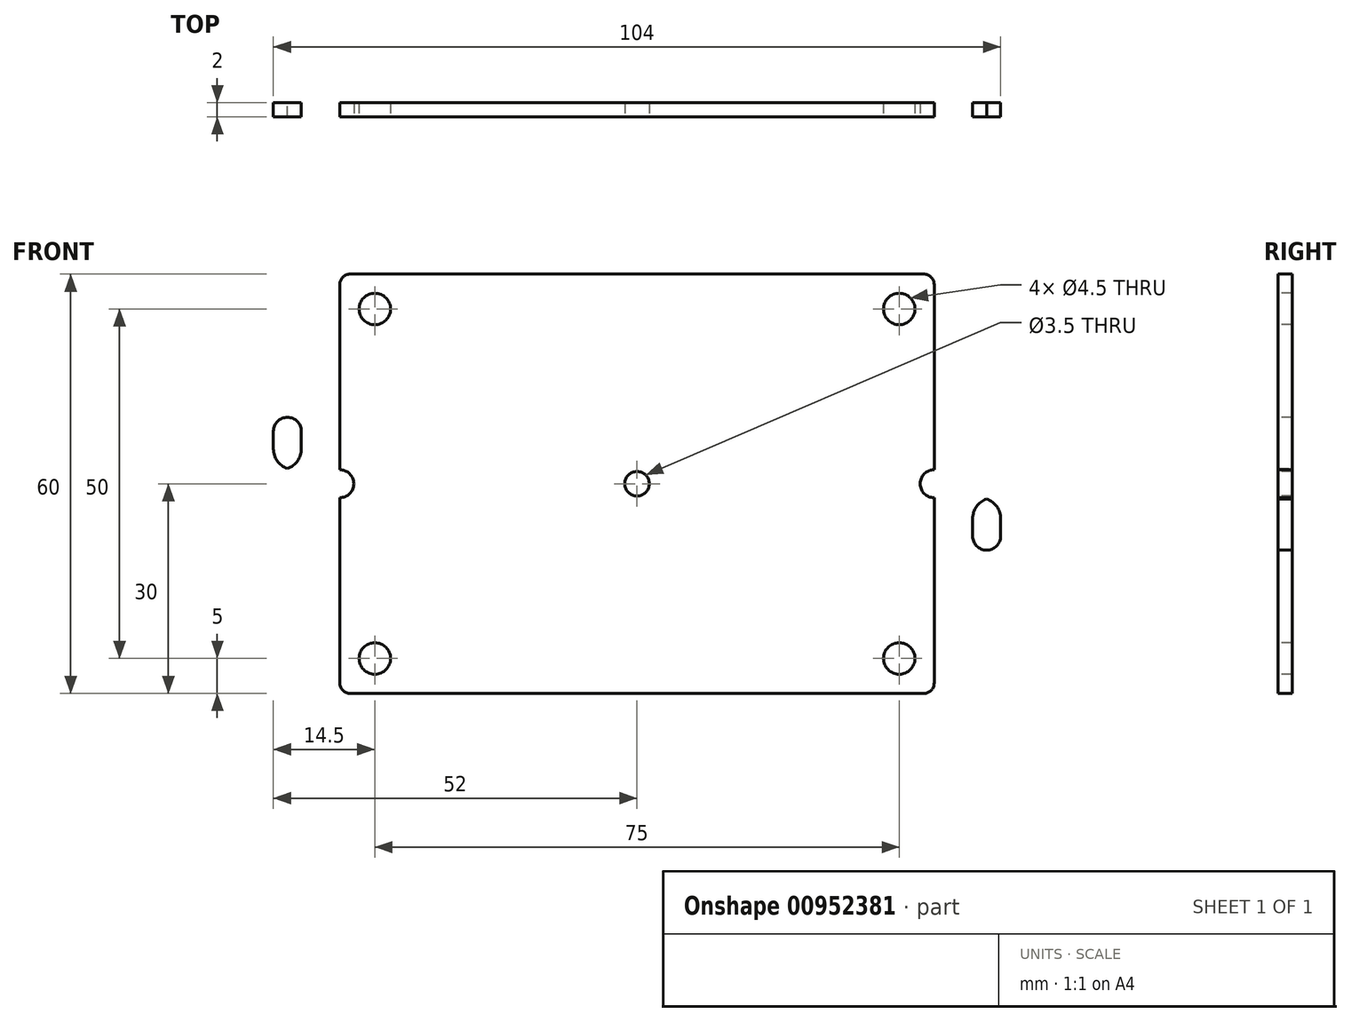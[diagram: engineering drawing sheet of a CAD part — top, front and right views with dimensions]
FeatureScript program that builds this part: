
annotation { "Feature Type Name" : "Feature", "Feature Type Description" : "" }
export const myFeature = defineFeature(function(context is Context, id is Id, definition is map)
    precondition{}
    {
        {
            var Q0;
            Q0=qCreatedBy(makeId("Front.planeOp"),FACE);
            var sketch = newSketch(context, id + "F0", { "sketchPlane" : qUnion([Q0])});
            skLineSegment(sketch, "E0.bottom", {"start": v(-42.5, -30) * mm, "end": v(42.5, -30) * mm});
            skLineSegment(sketch, "E0.top", {"start": v(-42.5, 30) * mm, "end": v(42.5, 30) * mm});
            skLineSegment(sketch, "E0.left", {"start": v(-42.5, -30) * mm, "end": v(-42.5, 30) * mm});
            skLineSegment(sketch, "E0.right", {"start": v(42.5, -30) * mm, "end": v(42.5, 30) * mm});
            skCircle(sketch, "E1", {"center": v(-37.5, 25) * mm, "radius": 2.25 * mm});
            skCircle(sketch, "E2", {"center": v(37.5, 25) * mm, "radius": 2.25 * mm});
            skCircle(sketch, "E3", {"center": v(-37.5, -25) * mm, "radius": 2.25 * mm});
            skCircle(sketch, "E4", {"center": v(37.5, -25) * mm, "radius": 2.25 * mm});
            skCircle(sketch, "E5", {"center": v(0, 0) * mm, "radius": 1.75 * mm});
            skLineSegment(sketch, "E6", {"start": v(-50, 7.5) * mm, "end": v(-50, -7.5) * mm});
            skLineSegment(sketch, "E7", {"start": v(-57.5, 0) * mm, "end": v(-42.5, 0) * mm});
            skArc(sketch, "E8.0.startCap", {"start": v(-52, 7.5) * mm, "mid": v(-50, 9.5) * mm, "end": v(-48, 7.5) * mm});
            skArc(sketch, "E8.0.endCap", {"start": v(-48, -7.5) * mm, "mid": v(-50, -9.5) * mm, "end": v(-52, -7.5) * mm});
            skLineSegment(sketch, "E8.0.left", {"start": v(-48, 7.5) * mm, "end": v(-48, -7.5) * mm});
            skLineSegment(sketch, "E8.0.right", {"start": v(-52, 7.5) * mm, "end": v(-52, -7.5) * mm});
            skArc(sketch, "E8.1.startCap", {"start": v(-57.5, -2) * mm, "mid": v(-59.5, 0) * mm, "end": v(-57.5, 2) * mm});
            skArc(sketch, "E8.1.endCap", {"start": v(-42.5, 2) * mm, "mid": v(-40.5, 0) * mm, "end": v(-42.5, -2) * mm});
            skLineSegment(sketch, "E8.1.left", {"start": v(-57.5, 2) * mm, "end": v(-42.5, 2) * mm});
            skLineSegment(sketch, "E8.1.right", {"start": v(-57.5, -2) * mm, "end": v(-42.5, -2) * mm});
            skArc(sketch, "E9.1.0.0", {"start": v(52, -7.5) * mm, "mid": v(50, -9.5) * mm, "end": v(48, -7.5) * mm});
            skArc(sketch, "E9.1.0.1", {"start": v(48, 7.5) * mm, "mid": v(50, 9.5) * mm, "end": v(52, 7.5) * mm});
            skLineSegment(sketch, "E9.1.0.2", {"start": v(52, 7.5) * mm, "end": v(52, -7.5) * mm});
            skLineSegment(sketch, "E9.1.0.3", {"start": v(42.5, 2) * mm, "end": v(57.5, 2) * mm});
            skLineSegment(sketch, "E9.1.0.4", {"start": v(42.5, -2) * mm, "end": v(57.5, -2) * mm});
            skLineSegment(sketch, "E9.1.0.5", {"start": v(42.5, 0) * mm, "end": v(57.5, 0) * mm});
            skLineSegment(sketch, "E9.1.0.6", {"start": v(48, 7.5) * mm, "end": v(48, -7.5) * mm});
            skArc(sketch, "E9.1.0.7", {"start": v(57.5, 2) * mm, "mid": v(59.5, 0) * mm, "end": v(57.5, -2) * mm});
            skLineSegment(sketch, "E9.1.0.8", {"start": v(50, 7.5) * mm, "end": v(50, -7.5) * mm});
            skArc(sketch, "E9.1.0.9", {"start": v(42.5, -2) * mm, "mid": v(40.5, 0) * mm, "end": v(42.5, 2) * mm});
            skLineSegment(sketch, "E9.direction1", {"start": v(-52, -7.5) * mm, "end": v(48, -7.5) * mm, "construction": true});
            skLineSegment(sketch, "E10.bottom", {"start": v(-65, 15) * mm, "end": v(65, 15) * mm});
            skLineSegment(sketch, "E10.top", {"start": v(-65, -15) * mm, "end": v(65, -15) * mm});
            skLineSegment(sketch, "E10.left", {"start": v(-65, 15) * mm, "end": v(-65, -15) * mm});
            skLineSegment(sketch, "E10.right", {"start": v(65, 15) * mm, "end": v(65, -15) * mm});
            skSolve(sketch);
        }
        {
            var Q0;
            Q0=makeQuery(id+"F0.imprint","IMPRINT",FACE,{"disambiguationData":[TD([[makeQuery(id+"F0.imprint","IMPRINT",EDGE,{"derivedFrom":sQuery(id+"F0.wireOp",EDGE,"E2")}),-1.0]])]});
            var Q1;
            Q1=makeQuery(id+"F0.imprint","IMPRINT",FACE,{"disambiguationData":[TD([[makeQuery(id+"F0.imprint","IMPRINT",EDGE,{"derivedFrom":sQuery(id+"F0.wireOp",EDGE,"E4")}),-1.0]])]});
            var Q2;
            {var subQ0=sQuery(id+"F0.wireOp",EDGE,"rjaW78t7-ypJx-lVJN-FZRe-d6buYRmC77cn");Q2=makeQuery(id+"F0.imprint","IMPRINT",FACE,{"disambiguationData":[TD([[makeQuery(id+"F0.imprint","IMPRINT",EDGE,{"derivedFrom":subQ0}),-1.0]])]});}
            var Q3;
            {var subQ0=sQuery(id+"F0.wireOp",EDGE,"1NJd6Qoc-oje8-l9O0-L9cF-t73cIRtufikx");Q3=makeQuery(id+"F0.imprint","IMPRINT",FACE,{"disambiguationData":[TD([[makeQuery(id+"F0.imprint","IMPRINT",EDGE,{"derivedFrom":subQ0}),1.0]])]});}
            var Q4;
            Q4=makeQuery(id+"F0.imprint","IMPRINT",FACE,{"disambiguationData":[TD([[makeQuery(id+"F0.imprint","IMPRINT",EDGE,{"derivedFrom":sQuery(id+"F0.wireOp",EDGE,"E3OZl69u-UJ4j-6qNk-wf2I-6YzBL0ODdr67")}),-1.0]])]});
            var Q5;
            {var subQ0=sQuery(id+"F0.wireOp",EDGE,"PN9uGExE-e6ce-JM7U-WgBa-r8B8Oa9EvhlK");var subQ1=sQuery(id+"F0.wireOp",EDGE,"r9N8xMkt-jfr5-NPvg-kqhV-x66qSIRX31zV");var subQ2=makeQuery(id+"F0.imprint","INTERSECT",VERTEX,{"disambiguationData":[OD(0.0)],"derivedFrom":[subQ1,subQ0]});Q5=makeQuery(id+"F0.imprint","IMPRINT",FACE,{"disambiguationData":[TD([[makeQuery(id+"F0.imprint","IMPRINT",EDGE,{"disambiguationData":[TD([[subQ2,-1.0]])],"derivedFrom":subQ0}),1.0]])]});}
            var Q6;
            {var subQ0=sQuery(id+"F0.wireOp",EDGE,"PN9uGExE-e6ce-JM7U-WgBa-r8B8Oa9EvhlK");var subQ1=sQuery(id+"F0.wireOp",EDGE,"r9N8xMkt-jfr5-NPvg-kqhV-x66qSIRX31zV");var subQ2=makeQuery(id+"F0.imprint","INTERSECT",VERTEX,{"disambiguationData":[OD(1.0)],"derivedFrom":[subQ1,subQ0]});Q6=makeQuery(id+"F0.imprint","IMPRINT",FACE,{"disambiguationData":[TD([[makeQuery(id+"F0.imprint","IMPRINT",EDGE,{"disambiguationData":[TD([[subQ2,1.0]])],"derivedFrom":subQ0}),1.0]])]});}
            var Q7;
            {var subQ0=sQuery(id+"F0.wireOp",EDGE,"9v4P5pMU-RGOu-vqJf-tuKl-UVKpjkJdRUzS");var subQ1=sQuery(id+"F0.wireOp",EDGE,"65dx6mvX-bEGy-U7NT-FcBn-9mAAU7fRP4gA");var subQ2=makeQuery(id+"F0.imprint","INTERSECT",VERTEX,{"disambiguationData":[OD(1.0)],"derivedFrom":[subQ1,subQ0]});Q7=makeQuery(id+"F0.imprint","IMPRINT",FACE,{"disambiguationData":[TD([[makeQuery(id+"F0.imprint","IMPRINT",EDGE,{"disambiguationData":[TD([[subQ2,-1.0]])],"derivedFrom":subQ1}),-1.0]])]});}
            var Q8;
            {var subQ0=sQuery(id+"F0.wireOp",EDGE,"9v4P5pMU-RGOu-vqJf-tuKl-UVKpjkJdRUzS");var subQ1=sQuery(id+"F0.wireOp",EDGE,"65dx6mvX-bEGy-U7NT-FcBn-9mAAU7fRP4gA");var subQ2=makeQuery(id+"F0.imprint","INTERSECT",VERTEX,{"disambiguationData":[OD(1.0)],"derivedFrom":[subQ1,subQ0]});Q8=makeQuery(id+"F0.imprint","IMPRINT",FACE,{"disambiguationData":[TD([[makeQuery(id+"F0.imprint","IMPRINT",EDGE,{"disambiguationData":[TD([[subQ2,-1.0]])],"derivedFrom":subQ1}),1.0]])]});}
            var Q9;
            {var subQ0=sQuery(id+"F0.wireOp",EDGE,"hM2ZLU3s-uU6V-4ag1-q0J9-zNWtTk9yT7fe");var subQ1=sQuery(id+"F0.wireOp",EDGE,"r9N8xMkt-jfr5-NPvg-kqhV-x66qSIRX31zV");var subQ2=makeQuery(id+"F0.imprint","INTERSECT",VERTEX,{"disambiguationData":[OD(1.0)],"derivedFrom":[subQ1,subQ0]});Q9=makeQuery(id+"F0.imprint","IMPRINT",FACE,{"disambiguationData":[TD([[makeQuery(id+"F0.imprint","IMPRINT",EDGE,{"disambiguationData":[TD([[subQ2,-1.0]])],"derivedFrom":subQ1}),-1.0]])]});}
            var Q10;
            {var subQ0=sQuery(id+"F0.wireOp",EDGE,"wBLZlDLe-3T5N-0JWb-rmkb-ln4iytn4BMBR");var subQ1=sQuery(id+"F0.wireOp",EDGE,"r9N8xMkt-jfr5-NPvg-kqhV-x66qSIRX31zV");var subQ2=makeQuery(id+"F0.imprint","INTERSECT",VERTEX,{"disambiguationData":[OD(1.0)],"derivedFrom":[subQ1,subQ0]});Q10=makeQuery(id+"F0.imprint","IMPRINT",FACE,{"disambiguationData":[TD([[makeQuery(id+"F0.imprint","IMPRINT",EDGE,{"disambiguationData":[TD([[subQ2,-1.0]])],"derivedFrom":subQ1}),-1.0]])]});}
            var Q11;
            {var subQ0=sQuery(id+"F0.wireOp",EDGE,"hM2ZLU3s-uU6V-4ag1-q0J9-zNWtTk9yT7fe");var subQ1=sQuery(id+"F0.wireOp",EDGE,"r9N8xMkt-jfr5-NPvg-kqhV-x66qSIRX31zV");var subQ2=makeQuery(id+"F0.imprint","INTERSECT",VERTEX,{"disambiguationData":[OD(0.0)],"derivedFrom":[subQ1,subQ0]});Q11=makeQuery(id+"F0.imprint","IMPRINT",FACE,{"disambiguationData":[TD([[makeQuery(id+"F0.imprint","IMPRINT",EDGE,{"disambiguationData":[TD([[subQ2,-1.0]])],"derivedFrom":subQ1}),-1.0]])]});}
            var Q12;
            {var subQ0=sQuery(id+"F0.wireOp",EDGE,"hM2ZLU3s-uU6V-4ag1-q0J9-zNWtTk9yT7fe");var subQ1=sQuery(id+"F0.wireOp",EDGE,"r9N8xMkt-jfr5-NPvg-kqhV-x66qSIRX31zV");var subQ2=makeQuery(id+"F0.imprint","INTERSECT",VERTEX,{"disambiguationData":[OD(0.0)],"derivedFrom":[subQ1,subQ0]});Q12=makeQuery(id+"F0.imprint","IMPRINT",FACE,{"disambiguationData":[TD([[makeQuery(id+"F0.imprint","IMPRINT",EDGE,{"disambiguationData":[TD([[subQ2,-1.0]])],"derivedFrom":subQ1}),1.0]])]});}
            var Q13;
            {var subQ0=sQuery(id+"F0.wireOp",EDGE,"wBLZlDLe-3T5N-0JWb-rmkb-ln4iytn4BMBR");var subQ1=sQuery(id+"F0.wireOp",EDGE,"r9N8xMkt-jfr5-NPvg-kqhV-x66qSIRX31zV");var subQ2=makeQuery(id+"F0.imprint","INTERSECT",VERTEX,{"disambiguationData":[OD(1.0)],"derivedFrom":[subQ1,subQ0]});Q13=makeQuery(id+"F0.imprint","IMPRINT",FACE,{"disambiguationData":[TD([[makeQuery(id+"F0.imprint","IMPRINT",EDGE,{"disambiguationData":[TD([[subQ2,-1.0]])],"derivedFrom":subQ1}),1.0]])]});}
            var Q14;
            {var subQ0=sQuery(id+"F0.wireOp",EDGE,"hM2ZLU3s-uU6V-4ag1-q0J9-zNWtTk9yT7fe");var subQ1=sQuery(id+"F0.wireOp",EDGE,"r9N8xMkt-jfr5-NPvg-kqhV-x66qSIRX31zV");var subQ2=makeQuery(id+"F0.imprint","INTERSECT",VERTEX,{"disambiguationData":[OD(0.0)],"derivedFrom":[subQ1,subQ0]});Q14=makeQuery(id+"F0.imprint","IMPRINT",FACE,{"disambiguationData":[TD([[makeQuery(id+"F0.imprint","IMPRINT",EDGE,{"disambiguationData":[TD([[subQ2,1.0]])],"derivedFrom":subQ1}),-1.0]])]});}
            var Q15;
            {var subQ0=sQuery(id+"F0.wireOp",EDGE,"hM2ZLU3s-uU6V-4ag1-q0J9-zNWtTk9yT7fe");var subQ1=sQuery(id+"F0.wireOp",EDGE,"r9N8xMkt-jfr5-NPvg-kqhV-x66qSIRX31zV");var subQ2=makeQuery(id+"F0.imprint","INTERSECT",VERTEX,{"disambiguationData":[OD(0.0)],"derivedFrom":[subQ1,subQ0]});Q15=makeQuery(id+"F0.imprint","IMPRINT",FACE,{"disambiguationData":[TD([[makeQuery(id+"F0.imprint","IMPRINT",EDGE,{"disambiguationData":[TD([[subQ2,1.0]])],"derivedFrom":subQ1}),1.0]])]});}
            var Q16;
            {var subQ0=sQuery(id+"F0.wireOp",EDGE,"tNTzekTW-7BOb-6XFC-JdlP-r3fOIQGOdmsq");var subQ1=sQuery(id+"F0.wireOp",EDGE,"65dx6mvX-bEGy-U7NT-FcBn-9mAAU7fRP4gA");var subQ2=makeQuery(id+"F0.imprint","INTERSECT",VERTEX,{"disambiguationData":[OD(0.0)],"derivedFrom":[subQ1,subQ0]});Q16=makeQuery(id+"F0.imprint","IMPRINT",FACE,{"disambiguationData":[TD([[makeQuery(id+"F0.imprint","IMPRINT",EDGE,{"disambiguationData":[TD([[subQ2,-1.0]])],"derivedFrom":subQ1}),1.0]])]});}
            var Q17;
            {var subQ0=sQuery(id+"F0.wireOp",EDGE,"tNTzekTW-7BOb-6XFC-JdlP-r3fOIQGOdmsq");var subQ1=sQuery(id+"F0.wireOp",EDGE,"65dx6mvX-bEGy-U7NT-FcBn-9mAAU7fRP4gA");var subQ2=makeQuery(id+"F0.imprint","INTERSECT",VERTEX,{"disambiguationData":[OD(0.0)],"derivedFrom":[subQ1,subQ0]});Q17=makeQuery(id+"F0.imprint","IMPRINT",FACE,{"disambiguationData":[TD([[makeQuery(id+"F0.imprint","IMPRINT",EDGE,{"disambiguationData":[TD([[subQ2,-1.0]])],"derivedFrom":subQ1}),-1.0]])]});}
            var Q18;
            {var subQ0=sQuery(id+"F0.wireOp",EDGE,"PN9uGExE-e6ce-JM7U-WgBa-r8B8Oa9EvhlK");var subQ1=sQuery(id+"F0.wireOp",EDGE,"r9N8xMkt-jfr5-NPvg-kqhV-x66qSIRX31zV");var subQ2=makeQuery(id+"F0.imprint","INTERSECT",VERTEX,{"disambiguationData":[OD(0.0)],"derivedFrom":[subQ1,subQ0]});Q18=makeQuery(id+"F0.imprint","IMPRINT",FACE,{"disambiguationData":[TD([[makeQuery(id+"F0.imprint","IMPRINT",EDGE,{"disambiguationData":[TD([[subQ2,-1.0]])],"derivedFrom":subQ1}),1.0]])]});}
            var Q19;
            {var subQ0=sQuery(id+"F0.wireOp",EDGE,"PN9uGExE-e6ce-JM7U-WgBa-r8B8Oa9EvhlK");var subQ1=sQuery(id+"F0.wireOp",EDGE,"r9N8xMkt-jfr5-NPvg-kqhV-x66qSIRX31zV");var subQ2=makeQuery(id+"F0.imprint","INTERSECT",VERTEX,{"disambiguationData":[OD(1.0)],"derivedFrom":[subQ1,subQ0]});Q19=makeQuery(id+"F0.imprint","IMPRINT",FACE,{"disambiguationData":[TD([[makeQuery(id+"F0.imprint","IMPRINT",EDGE,{"disambiguationData":[TD([[subQ2,1.0]])],"derivedFrom":subQ1}),1.0]])]});}
            var Q20;
            {var subQ0=sQuery(id+"F0.wireOp",EDGE,"hM2ZLU3s-uU6V-4ag1-q0J9-zNWtTk9yT7fe");var subQ1=sQuery(id+"F0.wireOp",EDGE,"r9N8xMkt-jfr5-NPvg-kqhV-x66qSIRX31zV");var subQ2=makeQuery(id+"F0.imprint","INTERSECT",VERTEX,{"disambiguationData":[OD(1.0)],"derivedFrom":[subQ1,subQ0]});Q20=makeQuery(id+"F0.imprint","IMPRINT",FACE,{"disambiguationData":[TD([[makeQuery(id+"F0.imprint","IMPRINT",EDGE,{"disambiguationData":[TD([[subQ2,-1.0]])],"derivedFrom":subQ1}),1.0]])]});}
            var Q21;
            Q21=makeQuery(id+"F0.imprint","IMPRINT",FACE,{"disambiguationData":[TD([[makeQuery(id+"F0.imprint","IMPRINT",EDGE,{"derivedFrom":sQuery(id+"F0.wireOp",EDGE,"E5")}),-1.0]])]});
            var Q22;
            {var subQ2=sQuery(id+"F0.wireOp",EDGE,"E8.0.startCap");Q22=makeQuery(id+"F0.imprint","IMPRINT",FACE,{"disambiguationData":[TD([[makeQuery(id+"F0.imprint","IMPRINT",EDGE,{"derivedFrom":subQ2}),1.0]])]});}
            var Q23;
            {var subQ7=sQuery(id+"F0.wireOp",EDGE,"E9.1.0.0");Q23=makeQuery(id+"F0.imprint","IMPRINT",FACE,{"disambiguationData":[TD([[makeQuery(id+"F0.imprint","IMPRINT",EDGE,{"derivedFrom":subQ7}),1.0]])]});}
            extrude(context, id + "F1", {"entities" : qUnion([Q0, Q1, Q2, Q3, Q4, Q5, Q6, Q7, Q8, Q9, Q10, Q11, Q12, Q13, Q14, Q15, Q16, Q17, Q18, Q19, Q20, Q21, Q22, Q23]), "oppositeDirection" : true, "depth" : 2 * mm, "offsetDistance" : 25 * mm});
        }
        {
            var Q0;
            Q0=makeQuery(id+"F1.opExtrude","SWEPT_EDGE",EDGE,{"disambiguationData":[OSD([sQuery(id+"F0.wireOp",EDGE,"E0.top"),sQuery(id+"F0.wireOp",EDGE,"E0.left")])]});
            var Q1;
            Q1=makeQuery(id+"F1.opExtrude","SWEPT_EDGE",EDGE,{"disambiguationData":[OSD([sQuery(id+"F0.wireOp",EDGE,"E0.top"),sQuery(id+"F0.wireOp",EDGE,"E0.right")])]});
            var Q2;
            Q2=makeQuery(id+"F1.opExtrude","SWEPT_EDGE",EDGE,{"disambiguationData":[OSD([sQuery(id+"F0.wireOp",EDGE,"E0.bottom"),sQuery(id+"F0.wireOp",EDGE,"E0.right")])]});
            var Q3;
            Q3=makeQuery(id+"F1.opExtrude","SWEPT_EDGE",EDGE,{"disambiguationData":[OSD([sQuery(id+"F0.wireOp",EDGE,"E0.bottom"),sQuery(id+"F0.wireOp",EDGE,"E0.left")])]});
            var Q4;
            Q4=makeQuery(id+"F1.opExtrude","SWEPT_EDGE",EDGE,{"disambiguationData":[OSD([sQuery(id+"F0.wireOp",EDGE,"E0.left"),sQuery(id+"F0.wireOp",EDGE,"E10.bottom")])]});
            var Q5;
            Q5=makeQuery(id+"F1.opExtrude","SWEPT_EDGE",EDGE,{"disambiguationData":[OSD([sQuery(id+"F0.wireOp",EDGE,"E10.bottom"),sQuery(id+"F0.wireOp",EDGE,"E10.left")])]});
            var Q6;
            Q6=makeQuery(id+"F1.opExtrude","SWEPT_EDGE",EDGE,{"disambiguationData":[OSD([sQuery(id+"F0.wireOp",EDGE,"E10.top"),sQuery(id+"F0.wireOp",EDGE,"E10.left")])]});
            var Q7;
            Q7=makeQuery(id+"F1.opExtrude","SWEPT_EDGE",EDGE,{"disambiguationData":[OSD([sQuery(id+"F0.wireOp",EDGE,"E0.left"),sQuery(id+"F0.wireOp",EDGE,"E10.top")])]});
            var Q8;
            Q8=makeQuery(id+"F1.opExtrude","SWEPT_EDGE",EDGE,{"disambiguationData":[OSD([sQuery(id+"F0.wireOp",EDGE,"E0.right"),sQuery(id+"F0.wireOp",EDGE,"E10.bottom")])]});
            var Q9;
            Q9=makeQuery(id+"F1.opExtrude","SWEPT_EDGE",EDGE,{"disambiguationData":[OSD([sQuery(id+"F0.wireOp",EDGE,"E10.bottom"),sQuery(id+"F0.wireOp",EDGE,"E10.right")])]});
            var Q10;
            Q10=makeQuery(id+"F1.opExtrude","SWEPT_EDGE",EDGE,{"disambiguationData":[OSD([sQuery(id+"F0.wireOp",EDGE,"E0.right"),sQuery(id+"F0.wireOp",EDGE,"E10.top")])]});
            var Q11;
            Q11=makeQuery(id+"F1.opExtrude","SWEPT_EDGE",EDGE,{"disambiguationData":[OSD([sQuery(id+"F0.wireOp",EDGE,"E10.top"),sQuery(id+"F0.wireOp",EDGE,"E10.right")])]});
            fillet(context, id + "F2", {"entities" : qUnion([Q0, Q1, Q2, Q3, Q4, Q5, Q6, Q7, Q8, Q9, Q10, Q11]), "radius" : 1.5 * mm, "tangentPropagation" : true, "allowEdgeOverflow" : false});
        }
        {
            var Q0;
            Q0=makeQuery(id+"F1.opExtrude","SWEPT_EDGE",EDGE,{"disambiguationData":[OSD([sQuery(id+"F0.wireOp",EDGE,"E9.1.0.3"),sQuery(id+"F0.wireOp",EDGE,"E9.1.0.6")])]});
            var Q1;
            Q1=makeQuery(id+"F1.opExtrude","SWEPT_EDGE",EDGE,{"disambiguationData":[OSD([sQuery(id+"F0.wireOp",EDGE,"E9.1.0.2"),sQuery(id+"F0.wireOp",EDGE,"E9.1.0.3")])]});
            var Q2;
            Q2=makeQuery(id+"F1.opExtrude","SWEPT_EDGE",EDGE,{"disambiguationData":[OSD([sQuery(id+"F0.wireOp",EDGE,"E9.1.0.4"),sQuery(id+"F0.wireOp",EDGE,"E9.1.0.6")])]});
            var Q3;
            Q3=makeQuery(id+"F1.opExtrude","SWEPT_EDGE",EDGE,{"disambiguationData":[OSD([sQuery(id+"F0.wireOp",EDGE,"E9.1.0.2"),sQuery(id+"F0.wireOp",EDGE,"E9.1.0.4")])]});
            var Q4;
            Q4=makeQuery(id+"F1.opExtrude","SWEPT_EDGE",EDGE,{"disambiguationData":[OSD([sQuery(id+"F0.wireOp",EDGE,"E8.0.left"),sQuery(id+"F0.wireOp",EDGE,"E8.1.left")])]});
            var Q5;
            Q5=makeQuery(id+"F1.opExtrude","SWEPT_EDGE",EDGE,{"disambiguationData":[OSD([sQuery(id+"F0.wireOp",EDGE,"E8.0.right"),sQuery(id+"F0.wireOp",EDGE,"E8.1.left")])]});
            var Q6;
            Q6=makeQuery(id+"F1.opExtrude","SWEPT_EDGE",EDGE,{"disambiguationData":[OSD([sQuery(id+"F0.wireOp",EDGE,"E8.0.left"),sQuery(id+"F0.wireOp",EDGE,"E8.1.right")])]});
            var Q7;
            Q7=makeQuery(id+"F1.opExtrude","SWEPT_EDGE",EDGE,{"disambiguationData":[OSD([sQuery(id+"F0.wireOp",EDGE,"E8.0.right"),sQuery(id+"F0.wireOp",EDGE,"E8.1.right")])]});
            fillet(context, id + "F3", {"entities" : qUnion([Q0, Q1, Q2, Q3, Q4, Q5, Q6, Q7]), "radius" : 3 * mm, "tangentPropagation" : true, "allowEdgeOverflow" : false});
        }
    });
